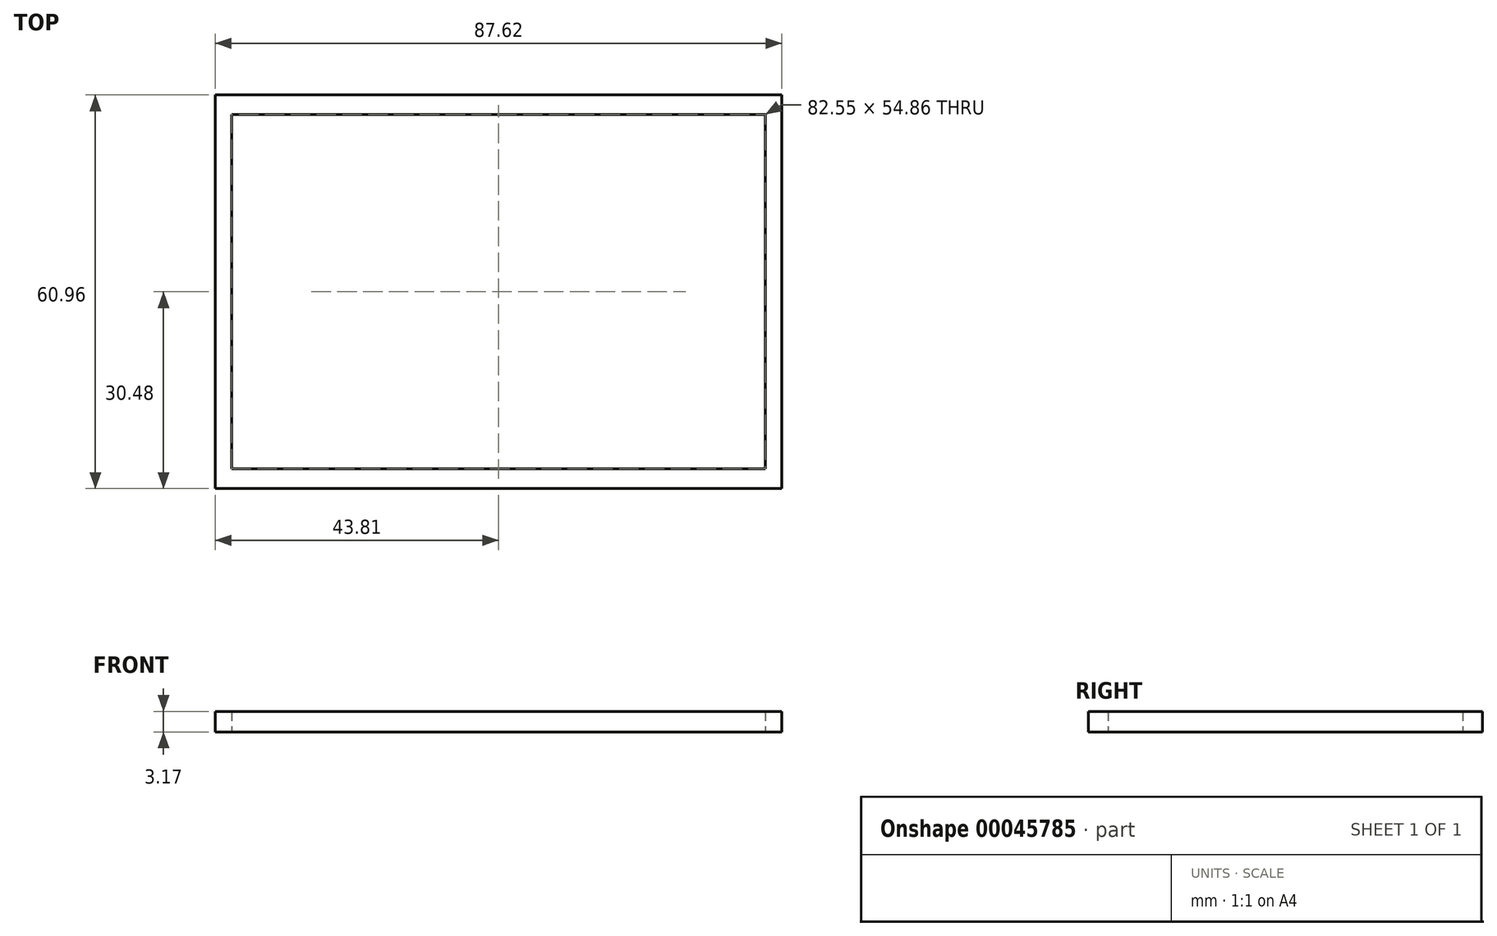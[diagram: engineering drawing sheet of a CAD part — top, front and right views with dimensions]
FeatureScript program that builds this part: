
annotation { "Feature Type Name" : "Feature", "Feature Type Description" : "" }
export const myFeature = defineFeature(function(context is Context, id is Id, definition is map)
    precondition{}
    {
        {
            var Q0;
            Q0=qCreatedBy(makeId("Top.planeOp"),FACE);
            var sketch = newSketch(context, id + "F0", { "sketchPlane" : qUnion([Q0])});
            skLineSegment(sketch, "E0.rect.bottom", {"start": v(-41.27, 27.43) * mm, "end": v(41.28, 27.43) * mm});
            skLineSegment(sketch, "E0.rect.top", {"start": v(-41.28, -27.43) * mm, "end": v(41.27, -27.43) * mm});
            skLineSegment(sketch, "E0.rect.left", {"start": v(-41.27, 27.43) * mm, "end": v(-41.28, -27.43) * mm});
            skLineSegment(sketch, "E0.rect.right", {"start": v(41.28, 27.43) * mm, "end": v(41.27, -27.43) * mm});
            skPoint(sketch, "E0.rect.middle", {"position": v(0, 0) * mm});
            skLineSegment(sketch, "E1.rect.bottom", {"start": v(-43.82, 30.48) * mm, "end": v(43.82, 30.48) * mm});
            skLineSegment(sketch, "E1.rect.top", {"start": v(-43.82, -30.48) * mm, "end": v(43.82, -30.48) * mm});
            skLineSegment(sketch, "E1.rect.left", {"start": v(-43.82, 30.48) * mm, "end": v(-43.82, -30.48) * mm});
            skLineSegment(sketch, "E1.rect.right", {"start": v(43.82, 30.48) * mm, "end": v(43.82, -30.48) * mm});
            skSolve(sketch);
        }
        {
            var Q0;
            Q0 = qSketchRegion(id + "F0", true);
            extrude(context, id + "F1", {"entities" : qUnion([Q0]), "depth" : 3.17 * mm});
        }
    });
